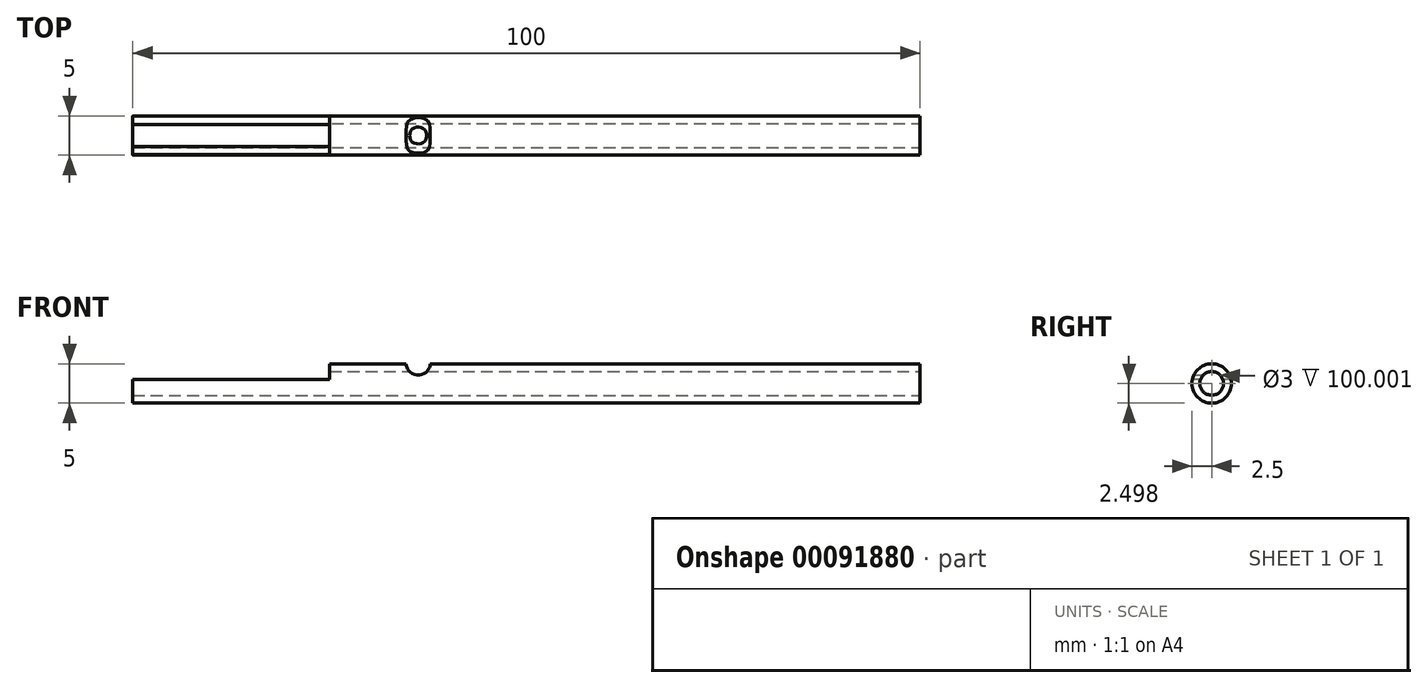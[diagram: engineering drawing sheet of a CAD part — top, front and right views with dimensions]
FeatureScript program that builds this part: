
annotation { "Feature Type Name" : "Feature", "Feature Type Description" : "" }
export const myFeature = defineFeature(function(context is Context, id is Id, definition is map)
    precondition{}
    {
        {
            var Q0;
            Q0=qCreatedBy(makeId("Front.planeOp"),FACE);
            var sketch = newSketch(context, id + "F0", { "sketchPlane" : qUnion([Q0])});
            skLineSegment(sketch, "E0.bottom", {"start": v(-37.97, 16.28) * mm, "end": v(62.03, 16.28) * mm});
            skLineSegment(sketch, "E0.top", {"start": v(-37.97, 15.28) * mm, "end": v(62.03, 15.28) * mm});
            skLineSegment(sketch, "E0.left", {"start": v(-37.97, 16.28) * mm, "end": v(-37.97, 15.28) * mm});
            skLineSegment(sketch, "E0.right", {"start": v(62.03, 16.28) * mm, "end": v(62.03, 15.28) * mm});
            skLineSegment(sketch, "E1", {"start": v(62.03, 16.28) * mm, "end": v(62.03, 13.78) * mm});
            skLineSegment(sketch, "E2", {"start": v(62.03, 13.78) * mm, "end": v(-46, 13.78) * mm});
            skPoint(sketch, "E3", {"position": v(62.03, 17.01) * mm});
            skSolve(sketch);
        }
        {
            var Q0;
            {var subQ0=sQuery(id+"F0.wireOp",EDGE,"E0.bottom");Q0=makeQuery(id+"F0.imprint","IMPRINT",FACE,{"disambiguationData":[TD([[makeQuery(id+"F0.imprint","IMPRINT",EDGE,{"derivedFrom":subQ0}),-1.0]])]});}
            var Q1;
            Q1=sQuery(id+"F0.wireOp",EDGE,"E2");
            revolve(context, id + "F1", {"entities" : qUnion([Q0]), "axis" : qUnion([Q1]), "revolveType" : RevolveType.FULL});
        }
        {
            var Q0;
            Q0=qCreatedBy(makeId("Front.planeOp"),FACE);
            var sketch = newSketch(context, id + "F2", { "sketchPlane" : qUnion([Q0])});
            skPoint(sketch, "E4", {"position": v(-37.97, 16.1) * mm});
            skSolve(sketch);
        }
        {
            var Q0;
            Q0=sQuery(id+"F2.wireOp",VERTEX,"E4");
            var Q1;
            Q1=makeQuery(id+"F1.opRevolve","SWEPT_FACE",FACE,{"disambiguationData":[OSD([sQuery(id+"F0.wireOp",EDGE,"E0.bottom")])]});
            cPlane(context, id + "F3", {"entities" : qUnion([Q0, Q1]), "cplaneType" : CPlaneType.LINE_POINT, "offset" : 150 * mm, "width" : 150 * mm, "height" : 150 * mm});
        }
        {
            var Q0;
            Q0=qCreatedBy(id+"F3.planeOp",FACE);
            var sketch = newSketch(context, id + "F4", { "sketchPlane" : qUnion([Q0])});
            skLineSegment(sketch, "E5.bottom", {"start": v(5.1, 14.27) * mm, "end": v(-4.4, 14.27) * mm});
            skLineSegment(sketch, "E5.top", {"start": v(5.1, 19.22) * mm, "end": v(-4.4, 19.22) * mm});
            skLineSegment(sketch, "E5.left", {"start": v(5.1, 14.27) * mm, "end": v(5.1, 19.22) * mm});
            skLineSegment(sketch, "E5.right", {"start": v(-4.4, 14.27) * mm, "end": v(-4.4, 19.22) * mm});
            skSolve(sketch);
        }
        {
            var Q0;
            Q0 = qSketchRegion(id + "F4", true);
            extrude(context, id + "F5", {"entities" : qUnion([Q0]), "operationType" : NewBodyOperationType.REMOVE, "depth" : 25 * mm});
        }
        {
            var Q0;
            Q0=qCreatedBy(makeId("Front.planeOp"),FACE);
            var sketch = newSketch(context, id + "F6", { "sketchPlane" : qUnion([Q0])});
            skCircle(sketch, "E6", {"center": v(-1.72, 16.4) * mm, "radius": 1.55 * mm});
            skSolve(sketch);
        }
        {
            var Q0;
            Q0 = qSketchRegion(id + "F6", true);
            extrude(context, id + "F7", {"entities" : qUnion([Q0]), "operationType" : NewBodyOperationType.REMOVE, "depth" : 25 * mm, "symmetric" : true});
        }
    });
